# Revit family: Seat-LaZBoy-Kascade Lounge-KAS23
name_source: partatom
category: Furniture
revit_build: Autodesk Revit 2017 (Build: 20160225_1515(x64)
units: mm (PartAtom-declared; Revit-internal decimal feet)

## family parameters
Always vertical = Yes
Cut with Voids When Loaded = No
OmniClass Number = 23.40.20.00
OmniClass Title = General Furniture and Specialties
Room Calculation Point = No
Shared = No
Work Plane-Based = No

## types (2) — shared parameters
Assembly Code = E2020200
Depth = 31.25"
Height = 31.75"
Manufacturer = LaZBoy
Product Documentation Link = URL
URL = https://www.la-z-boy.com
Width = 52.00"

## per-type parameters (varying)
| type | Description | Model | With Armcap |
| Upholstered Arms | 2 Seat Lounge Chair with Back Rail,  Upholstered Arms | KAS23F | No |
| Thermofoil Arm Caps | 2 Seat Lounge Chair with Back Rail, Thermofoil Arm Caps | KAS23A | Yes |

## geometry (parser evidence)
native form markers: Sweep x6
no freeform markers — native parametric forms only
